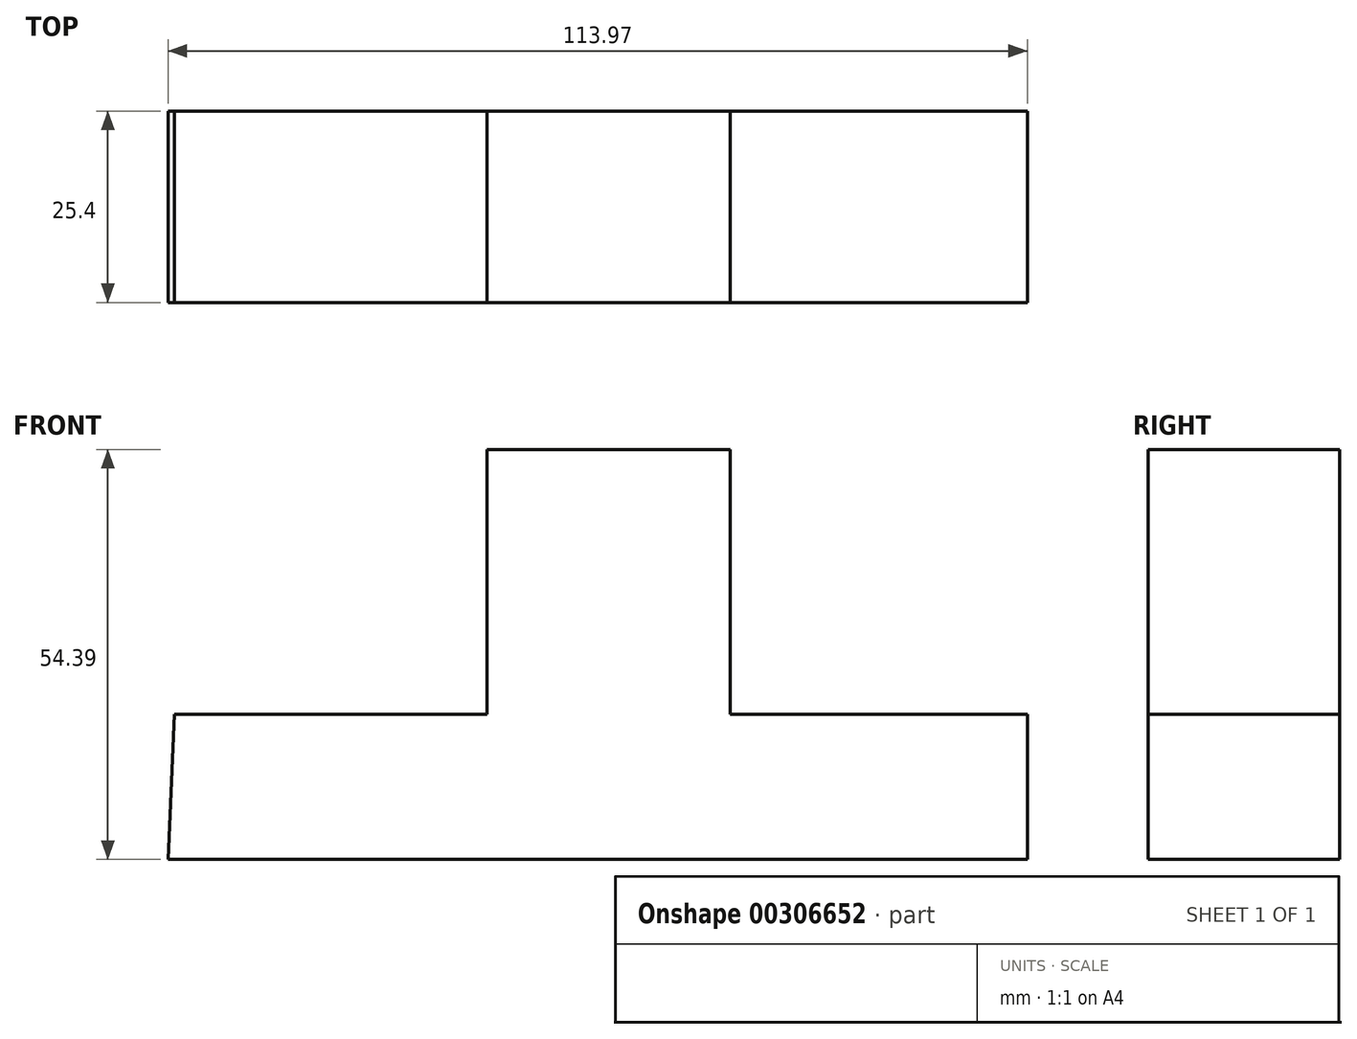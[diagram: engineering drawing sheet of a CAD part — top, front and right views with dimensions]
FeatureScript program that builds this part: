
annotation { "Feature Type Name" : "Feature", "Feature Type Description" : "" }
export const myFeature = defineFeature(function(context is Context, id is Id, definition is map)
    precondition{}
    {
        {
            var Q0;
            Q0=qCreatedBy(makeId("Front.planeOp"),FACE);
            var sketch = newSketch(context, id + "F0", { "sketchPlane" : qUnion([Q0])});
            skLineSegment(sketch, "E0", {"start": v(-59.29, 0) * mm, "end": v(-17.84, 0) * mm});
            skLineSegment(sketch, "E1", {"start": v(-17.84, 0) * mm, "end": v(-17.84, 35.11) * mm});
            skLineSegment(sketch, "E2", {"start": v(-17.84, 35.11) * mm, "end": v(14.4, 35.11) * mm});
            skLineSegment(sketch, "E3", {"start": v(14.4, 35.11) * mm, "end": v(14.4, 0) * mm});
            skLineSegment(sketch, "E4", {"start": v(14.4, 0) * mm, "end": v(53.82, 0) * mm});
            skLineSegment(sketch, "E5", {"start": v(53.82, 0) * mm, "end": v(53.82, -19.28) * mm});
            skLineSegment(sketch, "E6", {"start": v(53.82, -19.28) * mm, "end": v(-60.15, -19.28) * mm});
            skLineSegment(sketch, "E7", {"start": v(-60.15, -19.28) * mm, "end": v(-59.29, 0) * mm});
            skSolve(sketch);
        }
        {
            var Q0;
            Q0 = qSketchRegion(id + "F0", true);
            extrude(context, id + "F1", {"entities" : qUnion([Q0]), "depth" : 25.4 * mm});
        }
    });
